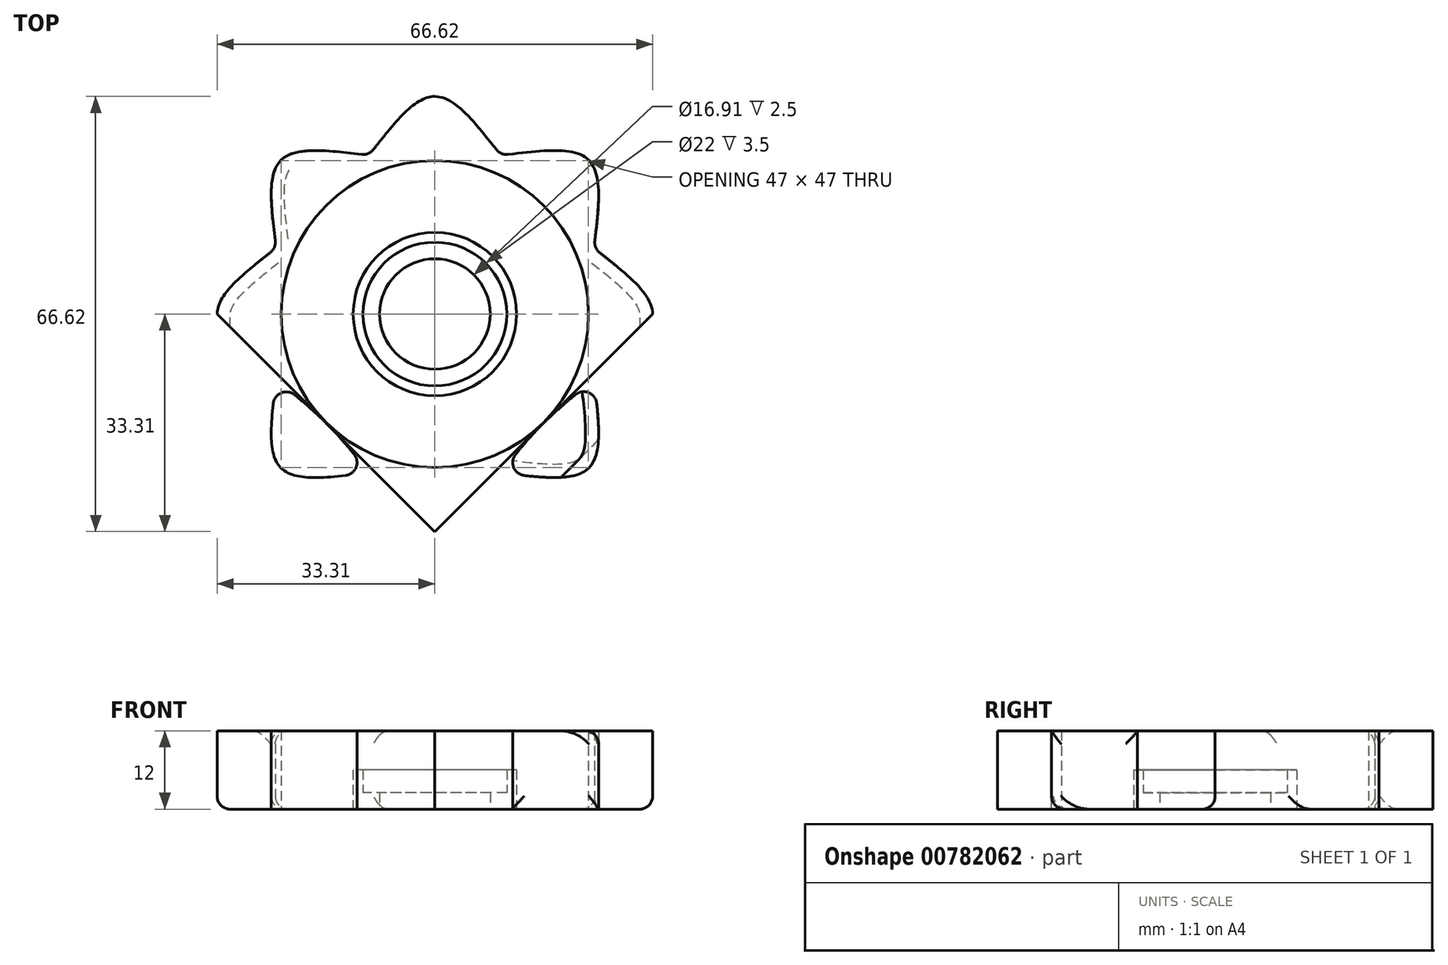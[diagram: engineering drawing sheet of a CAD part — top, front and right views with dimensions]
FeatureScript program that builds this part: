
annotation { "Feature Type Name" : "Feature", "Feature Type Description" : "" }
export const myFeature = defineFeature(function(context is Context, id is Id, definition is map)
    precondition{}
    {
        {
            var Q0;
            Q0=qCreatedBy(makeId("Top.planeOp"),FACE);
            var sketch = newSketch(context, id + "F0", { "sketchPlane" : qUnion([Q0])});
            skCircle(sketch, "E0", {"center": v(0, 0) * mm, "radius": 11 * mm});
            skCircle(sketch, "E1", {"center": v(0, 0) * mm, "radius": 23.5 * mm});
            skCircle(sketch, "E2", {"center": v(0, 0) * mm, "radius": 12.5 * mm});
            skCircle(sketch, "E3", {"center": v(0, 0) * mm, "radius": 33.31 * mm});
            skLineSegment(sketch, "E4", {"start": v(0, 33.31) * mm, "end": v(33.31, 0) * mm});
            skLineSegment(sketch, "E5", {"start": v(33.31, 0) * mm, "end": v(0, -33.31) * mm});
            skLineSegment(sketch, "E6", {"start": v(0, -33.31) * mm, "end": v(-33.31, 0) * mm});
            skLineSegment(sketch, "E7", {"start": v(-33.31, 0) * mm, "end": v(0, 33.31) * mm});
            skLineSegment(sketch, "E8", {"start": v(-16.66, 16.66) * mm, "end": v(-23.56, 23.56) * mm});
            skLineSegment(sketch, "E9", {"start": v(16.66, -16.66) * mm, "end": v(23.56, -23.56) * mm});
            skLineSegment(sketch, "E10", {"start": v(-16.66, -16.66) * mm, "end": v(-23.56, -23.56) * mm});
            skLineSegment(sketch, "E11", {"start": v(16.66, 16.66) * mm, "end": v(23.56, 23.56) * mm});
            skLineSegment(sketch, "E12", {"start": v(-33.31, 0) * mm, "end": v(-23.5, 0) * mm});
            skLineSegment(sketch, "E13", {"start": v(0, 33.31) * mm, "end": v(0, 23.5) * mm});
            skLineSegment(sketch, "E14", {"start": v(33.31, 0) * mm, "end": v(23.56, 0) * mm});
            skLineSegment(sketch, "E15", {"start": v(0, -33.31) * mm, "end": v(0, -23.5) * mm});
            skFitSpline(sketch, "E16", {"points": [v(0, 33.31) * mm, v(16.66, 16.66) * mm, v(33.31, 0) * mm, v(16.66, -16.66) * mm, v(0, -33.31) * mm, v(-16.66, -16.66) * mm, v(-33.31, 0) * mm, v(-16.66, 16.66) * mm, v(0, 33.31) * mm]});
            skFitSpline(sketch, "E17", {"points": [v(0, 23.5) * mm, v(23.56, 23.56) * mm, v(23.56, 0) * mm, v(23.56, -23.56) * mm, v(0, -23.5) * mm, v(-23.56, -23.56) * mm, v(-23.5, 0) * mm, v(-23.56, 23.56) * mm, v(0, 23.5) * mm]});
            skCircle(sketch, "E18", {"center": v(0, 0) * mm, "radius": 8.46 * mm});
            skSolve(sketch);
        }
        {
            var Q0;
            Q0=makeQuery(id+"F0.imprint","IMPRINT",FACE,{"disambiguationData":[TD([[makeQuery(id+"F0.imprint","IMPRINT",EDGE,{"derivedFrom":sQuery(id+"F0.wireOp",EDGE,"E0")}),-1.0]])]});
            var Q1;
            Q1=makeQuery(id+"F0.imprint","IMPRINT",FACE,{"disambiguationData":[TD([[makeQuery(id+"F0.imprint","IMPRINT",EDGE,{"derivedFrom":sQuery(id+"F0.wireOp",EDGE,"E0")}),1.0]])]});
            extrude(context, id + "F1", {"entities" : qUnion([Q0, Q1]), "depth" : 2.5 * mm, "offsetDistance" : 25.4 * mm});
        }
        {
            var Q0;
            {var subQ0=sQuery(id+"F0.wireOp",EDGE,"E17");var subQ3=sQuery(id+"F0.wireOp",EDGE,"E7");var subQ4=makeQuery(id+"F0.imprint","INTERSECT",VERTEX,{"disambiguationData":[OD(0.0)],"derivedFrom":[subQ3,subQ0]});Q0=makeQuery(id+"F0.imprint","IMPRINT",FACE,{"disambiguationData":[TD([[makeQuery(id+"F0.imprint","IMPRINT",EDGE,{"disambiguationData":[TD([[subQ4,-1.0]])],"derivedFrom":subQ3}),-1.0]])]});}
            var Q1;
            {var subQ0=sQuery(id+"F0.wireOp",EDGE,"E6");var subQ2=sQuery(id+"F0.wireOp",EDGE,"E17");var subQ6=makeQuery(id+"F0.imprint","INTERSECT",VERTEX,{"disambiguationData":[OD(0.0)],"derivedFrom":[subQ0,subQ2]});Q1=makeQuery(id+"F0.imprint","IMPRINT",FACE,{"disambiguationData":[TD([[makeQuery(id+"F0.imprint","IMPRINT",EDGE,{"disambiguationData":[TD([[subQ6,-1.0]])],"derivedFrom":subQ0}),-1.0]])]});}
            var Q2;
            {var subQ3=sQuery(id+"F0.wireOp",EDGE,"E17");var subQ5=makeQuery(id+"F0.imprint","INTERSECT",VERTEX,{"derivedFrom":[sQuery(id+"F0.wireOp",EDGE,"E14"),subQ3]});Q2=makeQuery(id+"F0.imprint","IMPRINT",FACE,{"disambiguationData":[TD([[makeQuery(id+"F0.imprint","IMPRINT",EDGE,{"disambiguationData":[TD([[subQ5,1.0]])],"derivedFrom":subQ3}),-1.0]])]});}
            var Q3;
            {var subQ0=sQuery(id+"F0.wireOp",EDGE,"E14");Q3=makeQuery(id+"F0.imprint","IMPRINT",FACE,{"disambiguationData":[TD([[makeQuery(id+"F0.imprint","IMPRINT",EDGE,{"derivedFrom":subQ0}),-1.0]])]});}
            var Q4;
            {var subQ0=sQuery(id+"F0.wireOp",EDGE,"E14");Q4=makeQuery(id+"F0.imprint","IMPRINT",FACE,{"disambiguationData":[TD([[makeQuery(id+"F0.imprint","IMPRINT",EDGE,{"derivedFrom":subQ0}),1.0]])]});}
            var Q5;
            {var subQ1=sQuery(id+"F0.wireOp",EDGE,"E5");var subQ3=sQuery(id+"F0.wireOp",EDGE,"E17");var subQ4=makeQuery(id+"F0.imprint","INTERSECT",VERTEX,{"disambiguationData":[OD(0.0)],"derivedFrom":[subQ1,subQ3]});Q5=makeQuery(id+"F0.imprint","IMPRINT",FACE,{"disambiguationData":[TD([[makeQuery(id+"F0.imprint","IMPRINT",EDGE,{"disambiguationData":[TD([[subQ4,-1.0]])],"derivedFrom":subQ3}),1.0]])]});}
            var Q6;
            {var subQ1=sQuery(id+"F0.wireOp",EDGE,"E4");var subQ3=sQuery(id+"F0.wireOp",EDGE,"E17");var subQ4=makeQuery(id+"F0.imprint","INTERSECT",VERTEX,{"disambiguationData":[OD(1.0)],"derivedFrom":[subQ1,subQ3]});Q6=makeQuery(id+"F0.imprint","IMPRINT",FACE,{"disambiguationData":[TD([[makeQuery(id+"F0.imprint","IMPRINT",EDGE,{"disambiguationData":[TD([[subQ4,1.0]])],"derivedFrom":subQ3}),1.0]])]});}
            var Q7;
            {var subQ1=sQuery(id+"F0.wireOp",EDGE,"E4");var subQ3=sQuery(id+"F0.wireOp",EDGE,"E17");var subQ4=makeQuery(id+"F0.imprint","INTERSECT",VERTEX,{"disambiguationData":[OD(1.0)],"derivedFrom":[subQ1,subQ3]});Q7=makeQuery(id+"F0.imprint","IMPRINT",FACE,{"disambiguationData":[TD([[makeQuery(id+"F0.imprint","IMPRINT",EDGE,{"disambiguationData":[TD([[subQ4,1.0]])],"derivedFrom":subQ3}),-1.0]])]});}
            var Q8;
            {var subQ1=sQuery(id+"F0.wireOp",EDGE,"E5");var subQ3=sQuery(id+"F0.wireOp",EDGE,"E17");var subQ4=makeQuery(id+"F0.imprint","INTERSECT",VERTEX,{"disambiguationData":[OD(0.0)],"derivedFrom":[subQ1,subQ3]});Q8=makeQuery(id+"F0.imprint","IMPRINT",FACE,{"disambiguationData":[TD([[makeQuery(id+"F0.imprint","IMPRINT",EDGE,{"disambiguationData":[TD([[subQ4,-1.0]])],"derivedFrom":subQ3}),-1.0]])]});}
            var Q9;
            {var subQ0=sQuery(id+"F0.wireOp",EDGE,"E9");Q9=makeQuery(id+"F0.imprint","IMPRINT",FACE,{"disambiguationData":[TD([[makeQuery(id+"F0.imprint","IMPRINT",EDGE,{"derivedFrom":subQ0}),1.0]])]});}
            var Q10;
            {var subQ0=sQuery(id+"F0.wireOp",EDGE,"E9");Q10=makeQuery(id+"F0.imprint","IMPRINT",FACE,{"disambiguationData":[TD([[makeQuery(id+"F0.imprint","IMPRINT",EDGE,{"derivedFrom":subQ0}),-1.0]])]});}
            var Q11;
            {var subQ1=sQuery(id+"F0.wireOp",EDGE,"E5");var subQ3=sQuery(id+"F0.wireOp",EDGE,"E17");var subQ4=makeQuery(id+"F0.imprint","INTERSECT",VERTEX,{"disambiguationData":[OD(1.0)],"derivedFrom":[subQ1,subQ3]});Q11=makeQuery(id+"F0.imprint","IMPRINT",FACE,{"disambiguationData":[TD([[makeQuery(id+"F0.imprint","IMPRINT",EDGE,{"disambiguationData":[TD([[subQ4,1.0]])],"derivedFrom":subQ3}),-1.0]])]});}
            var Q12;
            {var subQ0=sQuery(id+"F0.wireOp",EDGE,"E11");Q12=makeQuery(id+"F0.imprint","IMPRINT",FACE,{"disambiguationData":[TD([[makeQuery(id+"F0.imprint","IMPRINT",EDGE,{"derivedFrom":subQ0}),-1.0]])]});}
            var Q13;
            {var subQ0=sQuery(id+"F0.wireOp",EDGE,"E11");Q13=makeQuery(id+"F0.imprint","IMPRINT",FACE,{"disambiguationData":[TD([[makeQuery(id+"F0.imprint","IMPRINT",EDGE,{"derivedFrom":subQ0}),1.0]])]});}
            var Q14;
            {var subQ1=sQuery(id+"F0.wireOp",EDGE,"E4");var subQ3=sQuery(id+"F0.wireOp",EDGE,"E17");var subQ4=makeQuery(id+"F0.imprint","INTERSECT",VERTEX,{"disambiguationData":[OD(0.0)],"derivedFrom":[subQ1,subQ3]});Q14=makeQuery(id+"F0.imprint","IMPRINT",FACE,{"disambiguationData":[TD([[makeQuery(id+"F0.imprint","IMPRINT",EDGE,{"disambiguationData":[TD([[subQ4,-1.0]])],"derivedFrom":subQ3}),-1.0]])]});}
            var Q15;
            {var subQ1=sQuery(id+"F0.wireOp",EDGE,"E4");var subQ3=sQuery(id+"F0.wireOp",EDGE,"E17");var subQ4=makeQuery(id+"F0.imprint","INTERSECT",VERTEX,{"disambiguationData":[OD(0.0)],"derivedFrom":[subQ1,subQ3]});Q15=makeQuery(id+"F0.imprint","IMPRINT",FACE,{"disambiguationData":[TD([[makeQuery(id+"F0.imprint","IMPRINT",EDGE,{"disambiguationData":[TD([[subQ4,-1.0]])],"derivedFrom":subQ3}),1.0]])]});}
            var Q16;
            {var subQ0=sQuery(id+"F0.wireOp",EDGE,"E13");Q16=makeQuery(id+"F0.imprint","IMPRINT",FACE,{"disambiguationData":[TD([[makeQuery(id+"F0.imprint","IMPRINT",EDGE,{"derivedFrom":subQ0}),-1.0]])]});}
            var Q17;
            {var subQ0=sQuery(id+"F0.wireOp",EDGE,"E13");Q17=makeQuery(id+"F0.imprint","IMPRINT",FACE,{"disambiguationData":[TD([[makeQuery(id+"F0.imprint","IMPRINT",EDGE,{"derivedFrom":subQ0}),1.0]])]});}
            var Q18;
            {var subQ1=sQuery(id+"F0.wireOp",EDGE,"E7");var subQ3=sQuery(id+"F0.wireOp",EDGE,"E17");var subQ4=makeQuery(id+"F0.imprint","INTERSECT",VERTEX,{"disambiguationData":[OD(1.0)],"derivedFrom":[subQ1,subQ3]});Q18=makeQuery(id+"F0.imprint","IMPRINT",FACE,{"disambiguationData":[TD([[makeQuery(id+"F0.imprint","IMPRINT",EDGE,{"disambiguationData":[TD([[subQ4,1.0]])],"derivedFrom":subQ3}),1.0]])]});}
            var Q19;
            {var subQ1=sQuery(id+"F0.wireOp",EDGE,"E7");var subQ3=sQuery(id+"F0.wireOp",EDGE,"E17");var subQ4=makeQuery(id+"F0.imprint","INTERSECT",VERTEX,{"disambiguationData":[OD(1.0)],"derivedFrom":[subQ1,subQ3]});Q19=makeQuery(id+"F0.imprint","IMPRINT",FACE,{"disambiguationData":[TD([[makeQuery(id+"F0.imprint","IMPRINT",EDGE,{"disambiguationData":[TD([[subQ4,1.0]])],"derivedFrom":subQ3}),-1.0]])]});}
            var Q20;
            {var subQ0=sQuery(id+"F0.wireOp",EDGE,"E8");Q20=makeQuery(id+"F0.imprint","IMPRINT",FACE,{"disambiguationData":[TD([[makeQuery(id+"F0.imprint","IMPRINT",EDGE,{"derivedFrom":subQ0}),1.0]])]});}
            var Q21;
            {var subQ0=sQuery(id+"F0.wireOp",EDGE,"E8");Q21=makeQuery(id+"F0.imprint","IMPRINT",FACE,{"disambiguationData":[TD([[makeQuery(id+"F0.imprint","IMPRINT",EDGE,{"derivedFrom":subQ0}),-1.0]])]});}
            var Q22;
            {var subQ0=sQuery(id+"F0.wireOp",EDGE,"E10");Q22=makeQuery(id+"F0.imprint","IMPRINT",FACE,{"disambiguationData":[TD([[makeQuery(id+"F0.imprint","IMPRINT",EDGE,{"derivedFrom":subQ0}),-1.0]])]});}
            var Q23;
            {var subQ0=sQuery(id+"F0.wireOp",EDGE,"E10");Q23=makeQuery(id+"F0.imprint","IMPRINT",FACE,{"disambiguationData":[TD([[makeQuery(id+"F0.imprint","IMPRINT",EDGE,{"derivedFrom":subQ0}),1.0]])]});}
            var Q24;
            {var subQ1=sQuery(id+"F0.wireOp",EDGE,"E6");var subQ3=sQuery(id+"F0.wireOp",EDGE,"E17");var subQ4=makeQuery(id+"F0.imprint","INTERSECT",VERTEX,{"disambiguationData":[OD(1.0)],"derivedFrom":[subQ1,subQ3]});Q24=makeQuery(id+"F0.imprint","IMPRINT",FACE,{"disambiguationData":[TD([[makeQuery(id+"F0.imprint","IMPRINT",EDGE,{"disambiguationData":[TD([[subQ4,1.0]])],"derivedFrom":subQ3}),1.0]])]});}
            var Q25;
            {var subQ0=sQuery(id+"F0.wireOp",EDGE,"E12");Q25=makeQuery(id+"F0.imprint","IMPRINT",FACE,{"disambiguationData":[TD([[makeQuery(id+"F0.imprint","IMPRINT",EDGE,{"derivedFrom":subQ0}),-1.0]])]});}
            var Q26;
            {var subQ0=sQuery(id+"F0.wireOp",EDGE,"E12");Q26=makeQuery(id+"F0.imprint","IMPRINT",FACE,{"disambiguationData":[TD([[makeQuery(id+"F0.imprint","IMPRINT",EDGE,{"derivedFrom":subQ0}),1.0]])]});}
            var Q27;
            {var subQ1=sQuery(id+"F0.wireOp",EDGE,"E7");var subQ3=sQuery(id+"F0.wireOp",EDGE,"E17");var subQ4=makeQuery(id+"F0.imprint","INTERSECT",VERTEX,{"disambiguationData":[OD(0.0)],"derivedFrom":[subQ1,subQ3]});Q27=makeQuery(id+"F0.imprint","IMPRINT",FACE,{"disambiguationData":[TD([[makeQuery(id+"F0.imprint","IMPRINT",EDGE,{"disambiguationData":[TD([[subQ4,-1.0]])],"derivedFrom":subQ3}),1.0]])]});}
            var Q28;
            {var subQ1=sQuery(id+"F0.wireOp",EDGE,"E7");var subQ3=sQuery(id+"F0.wireOp",EDGE,"E17");var subQ4=makeQuery(id+"F0.imprint","INTERSECT",VERTEX,{"disambiguationData":[OD(0.0)],"derivedFrom":[subQ1,subQ3]});Q28=makeQuery(id+"F0.imprint","IMPRINT",FACE,{"disambiguationData":[TD([[makeQuery(id+"F0.imprint","IMPRINT",EDGE,{"disambiguationData":[TD([[subQ4,-1.0]])],"derivedFrom":subQ3}),-1.0]])]});}
            var Q29;
            {var subQ1=sQuery(id+"F0.wireOp",EDGE,"E6");var subQ3=sQuery(id+"F0.wireOp",EDGE,"E17");var subQ4=makeQuery(id+"F0.imprint","INTERSECT",VERTEX,{"disambiguationData":[OD(1.0)],"derivedFrom":[subQ1,subQ3]});Q29=makeQuery(id+"F0.imprint","IMPRINT",FACE,{"disambiguationData":[TD([[makeQuery(id+"F0.imprint","IMPRINT",EDGE,{"disambiguationData":[TD([[subQ4,1.0]])],"derivedFrom":subQ3}),-1.0]])]});}
            var Q30;
            {var subQ1=sQuery(id+"F0.wireOp",EDGE,"E6");var subQ3=sQuery(id+"F0.wireOp",EDGE,"E17");var subQ4=makeQuery(id+"F0.imprint","INTERSECT",VERTEX,{"disambiguationData":[OD(0.0)],"derivedFrom":[subQ1,subQ3]});Q30=makeQuery(id+"F0.imprint","IMPRINT",FACE,{"disambiguationData":[TD([[makeQuery(id+"F0.imprint","IMPRINT",EDGE,{"disambiguationData":[TD([[subQ4,-1.0]])],"derivedFrom":subQ3}),-1.0]])]});}
            var Q31;
            {var subQ0=sQuery(id+"F0.wireOp",EDGE,"E15");Q31=makeQuery(id+"F0.imprint","IMPRINT",FACE,{"disambiguationData":[TD([[makeQuery(id+"F0.imprint","IMPRINT",EDGE,{"derivedFrom":subQ0}),1.0]])]});}
            var Q32;
            {var subQ1=sQuery(id+"F0.wireOp",EDGE,"E6");var subQ3=sQuery(id+"F0.wireOp",EDGE,"E17");var subQ4=makeQuery(id+"F0.imprint","INTERSECT",VERTEX,{"disambiguationData":[OD(0.0)],"derivedFrom":[subQ1,subQ3]});Q32=makeQuery(id+"F0.imprint","IMPRINT",FACE,{"disambiguationData":[TD([[makeQuery(id+"F0.imprint","IMPRINT",EDGE,{"disambiguationData":[TD([[subQ4,-1.0]])],"derivedFrom":subQ3}),1.0]])]});}
            var Q33;
            {var subQ1=sQuery(id+"F0.wireOp",EDGE,"E5");var subQ3=sQuery(id+"F0.wireOp",EDGE,"E17");var subQ4=makeQuery(id+"F0.imprint","INTERSECT",VERTEX,{"disambiguationData":[OD(1.0)],"derivedFrom":[subQ1,subQ3]});Q33=makeQuery(id+"F0.imprint","IMPRINT",FACE,{"disambiguationData":[TD([[makeQuery(id+"F0.imprint","IMPRINT",EDGE,{"disambiguationData":[TD([[subQ4,1.0]])],"derivedFrom":subQ3}),1.0]])]});}
            var Q34;
            {var subQ0=sQuery(id+"F0.wireOp",EDGE,"E15");Q34=makeQuery(id+"F0.imprint","IMPRINT",FACE,{"disambiguationData":[TD([[makeQuery(id+"F0.imprint","IMPRINT",EDGE,{"derivedFrom":subQ0}),-1.0]])]});}
            extrude(context, id + "F2", {"entities" : qUnion([Q0, Q1, Q2, Q3, Q4, Q5, Q6, Q7, Q8, Q9, Q10, Q11, Q12, Q13, Q14, Q15, Q16, Q17, Q18, Q19, Q20, Q21, Q22, Q23, Q24, Q25, Q26, Q27, Q28, Q29, Q30, Q31, Q32, Q33, Q34]), "operationType" : NewBodyOperationType.ADD, "depth" : 12 * mm, "offsetDistance" : 25.4 * mm});
        }
        {
            var Q0;
            {var subQ0=sQuery(id+"F0.wireOp",EDGE,"E16");var subQ2=sQuery(id+"F0.wireOp",EDGE,"E17");Q0=makeQuery(id+"F2.opExtrude","CAP_EDGE",EDGE,{"disambiguationData":[OSD([subQ0]),TDD([makeQuery(id+"F0.imprint","IMPRINT",EDGE,{"disambiguationData":[TD([[makeQuery(id+"F0.imprint","INTERSECT",VERTEX,{"disambiguationData":[OD(1.0)],"derivedFrom":[subQ0,subQ2]}),-1.0]])],"derivedFrom":subQ0}),makeQuery(id+"F0.imprint","IMPRINT",EDGE,{"disambiguationData":[TD([[makeQuery(id+"F0.imprint","INTERSECT",VERTEX,{"disambiguationData":[OD(2.0)],"derivedFrom":[subQ0,subQ2]}),1.0]])],"derivedFrom":subQ0})])],"isStart":true});}
            var Q1;
            {var subQ0=sQuery(id+"F0.wireOp",EDGE,"E17");var subQ1=sQuery(id+"F0.wireOp",EDGE,"E3");var subQ3=sQuery(id+"F0.wireOp",EDGE,"E16");var subQ4=makeQuery(id+"F0.imprint","INTERSECT",VERTEX,{"disambiguationData":[OD(3.0)],"derivedFrom":[subQ1,subQ0]});Q1=makeQuery(id+"F2.opExtrude","CAP_EDGE",EDGE,{"disambiguationData":[OSD([subQ0]),TDD([makeQuery(id+"F0.imprint","IMPRINT",EDGE,{"disambiguationData":[TD([[subQ4,1.0]])],"derivedFrom":subQ0}),makeQuery(id+"F0.imprint","IMPRINT",EDGE,{"disambiguationData":[TD([[subQ4,-1.0]])],"derivedFrom":subQ0}),makeQuery(id+"F0.imprint","IMPRINT",EDGE,{"disambiguationData":[TD([[makeQuery(id+"F0.imprint","INTERSECT",VERTEX,{"disambiguationData":[OD(3.0)],"derivedFrom":[subQ3,subQ0]}),1.0]])],"derivedFrom":subQ0})])],"isStart":true});}
            var Q2;
            {var subQ0=sQuery(id+"F0.wireOp",EDGE,"E17");var subQ1=sQuery(id+"F0.wireOp",EDGE,"E16");Q2=makeQuery(id+"F2.opExtrude","SWEPT_EDGE",EDGE,{"disambiguationData":[OSD([subQ1,subQ0]),TDD([makeQuery(id+"F0.imprint","INTERSECT",VERTEX,{"disambiguationData":[OD(2.0)],"derivedFrom":[subQ1,subQ0]})])]});}
            var Q3;
            {var subQ0=sQuery(id+"F0.wireOp",EDGE,"E17");var subQ1=sQuery(id+"F0.wireOp",EDGE,"E16");Q3=makeQuery(id+"F2.opExtrude","SWEPT_EDGE",EDGE,{"disambiguationData":[OSD([subQ1,subQ0]),TDD([makeQuery(id+"F0.imprint","INTERSECT",VERTEX,{"disambiguationData":[OD(3.0)],"derivedFrom":[subQ1,subQ0]})])]});}
            var Q4;
            {var subQ0=sQuery(id+"F0.wireOp",EDGE,"E17");var subQ1=sQuery(id+"F0.wireOp",EDGE,"E16");Q4=makeQuery(id+"F2.opExtrude","SWEPT_EDGE",EDGE,{"disambiguationData":[OSD([subQ1,subQ0]),TDD([makeQuery(id+"F0.imprint","INTERSECT",VERTEX,{"disambiguationData":[OD(4.0)],"derivedFrom":[subQ1,subQ0]})])]});}
            var Q5;
            {var subQ0=sQuery(id+"F0.wireOp",EDGE,"E16");var subQ2=sQuery(id+"F0.wireOp",EDGE,"E17");Q5=makeQuery(id+"F2.opExtrude","CAP_EDGE",EDGE,{"disambiguationData":[OSD([subQ0]),TDD([makeQuery(id+"F0.imprint","IMPRINT",EDGE,{"disambiguationData":[TD([[makeQuery(id+"F0.imprint","INTERSECT",VERTEX,{"disambiguationData":[OD(5.0)],"derivedFrom":[subQ0,subQ2]}),-1.0]])],"derivedFrom":subQ0}),makeQuery(id+"F0.imprint","IMPRINT",EDGE,{"disambiguationData":[TD([[makeQuery(id+"F0.imprint","INTERSECT",VERTEX,{"disambiguationData":[OD(6.0)],"derivedFrom":[subQ0,subQ2]}),1.0]])],"derivedFrom":subQ0})])],"isStart":true});}
            var Q6;
            {var subQ0=sQuery(id+"F0.wireOp",EDGE,"E17");var subQ1=sQuery(id+"F0.wireOp",EDGE,"E16");Q6=makeQuery(id+"F2.opExtrude","SWEPT_EDGE",EDGE,{"disambiguationData":[OSD([subQ1,subQ0]),TDD([makeQuery(id+"F0.imprint","INTERSECT",VERTEX,{"disambiguationData":[OD(6.0)],"derivedFrom":[subQ1,subQ0]})])]});}
            var Q7;
            {var subQ0=sQuery(id+"F0.wireOp",EDGE,"E17");var subQ1=sQuery(id+"F0.wireOp",EDGE,"E16");Q7=makeQuery(id+"F2.opExtrude","SWEPT_EDGE",EDGE,{"disambiguationData":[OSD([subQ1,subQ0]),TDD([makeQuery(id+"F0.imprint","INTERSECT",VERTEX,{"disambiguationData":[OD(5.0)],"derivedFrom":[subQ1,subQ0]})])]});}
            var Q8;
            {var subQ0=sQuery(id+"F0.wireOp",EDGE,"E17");var subQ1=sQuery(id+"F0.wireOp",EDGE,"E16");Q8=makeQuery(id+"F2.opExtrude","SWEPT_EDGE",EDGE,{"disambiguationData":[OSD([subQ1,subQ0]),TDD([makeQuery(id+"F0.imprint","INTERSECT",VERTEX,{"disambiguationData":[OD(7.0)],"derivedFrom":[subQ1,subQ0]})])]});}
            var Q9;
            {var subQ0=sQuery(id+"F0.wireOp",EDGE,"E17");var subQ1=sQuery(id+"F0.wireOp",EDGE,"E16");Q9=makeQuery(id+"F2.opExtrude","SWEPT_EDGE",EDGE,{"disambiguationData":[OSD([subQ1,subQ0]),TDD([makeQuery(id+"F0.imprint","INTERSECT",VERTEX,{"disambiguationData":[OD(0.0)],"derivedFrom":[subQ1,subQ0]})])]});}
            var Q10;
            {var subQ0=sQuery(id+"F0.wireOp",EDGE,"E17");var subQ1=sQuery(id+"F0.wireOp",EDGE,"E16");Q10=makeQuery(id+"F2.opExtrude","SWEPT_EDGE",EDGE,{"disambiguationData":[OSD([subQ1,subQ0]),TDD([makeQuery(id+"F0.imprint","INTERSECT",VERTEX,{"disambiguationData":[OD(1.0)],"derivedFrom":[subQ1,subQ0]})])]});}
            var Q11;
            {var subQ0=sQuery(id+"F0.wireOp",EDGE,"E17");var subQ1=sQuery(id+"F0.wireOp",EDGE,"E3");var subQ3=sQuery(id+"F0.wireOp",EDGE,"E16");var subQ4=makeQuery(id+"F0.imprint","INTERSECT",VERTEX,{"disambiguationData":[OD(1.0)],"derivedFrom":[subQ1,subQ0]});Q11=makeQuery(id+"F2.opExtrude","CAP_EDGE",EDGE,{"disambiguationData":[OSD([subQ0]),TDD([makeQuery(id+"F0.imprint","IMPRINT",EDGE,{"disambiguationData":[TD([[subQ4,1.0]])],"derivedFrom":subQ0}),makeQuery(id+"F0.imprint","IMPRINT",EDGE,{"disambiguationData":[TD([[subQ4,-1.0]])],"derivedFrom":subQ0}),makeQuery(id+"F0.imprint","IMPRINT",EDGE,{"disambiguationData":[TD([[makeQuery(id+"F0.imprint","INTERSECT",VERTEX,{"disambiguationData":[OD(7.0)],"derivedFrom":[subQ3,subQ0]}),1.0]])],"derivedFrom":subQ0})])],"isStart":false});}
            fillet(context, id + "F3", {"entities" : qUnion([Q0, Q1, Q2, Q3, Q4, Q5, Q6, Q7, Q8, Q9, Q10, Q11]), "radius" : 2 * mm, "tangentPropagation" : true, "allowEdgeOverflow" : false});
        }
        {
            var Q0;
            Q0=makeQuery(id+"F0.imprint","IMPRINT",FACE,{"disambiguationData":[TD([[makeQuery(id+"F0.imprint","IMPRINT",EDGE,{"derivedFrom":sQuery(id+"F0.wireOp",EDGE,"E0")}),-1.0]])]});
            extrude(context, id + "F4", {"entities" : qUnion([Q0]), "operationType" : NewBodyOperationType.ADD, "depth" : 6 * mm, "offsetDistance" : 25.4 * mm});
        }
    });
